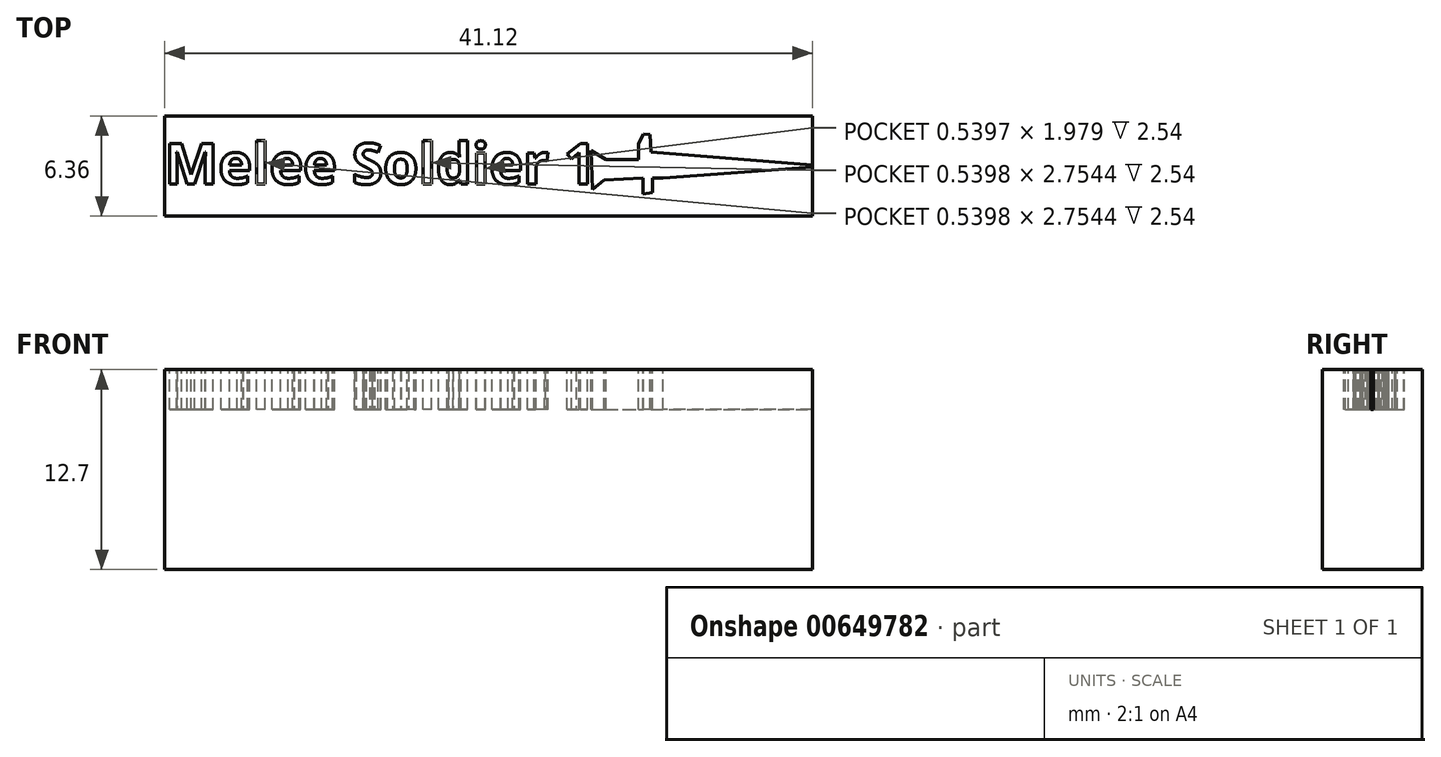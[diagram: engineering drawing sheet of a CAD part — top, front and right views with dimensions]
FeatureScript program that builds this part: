
annotation { "Feature Type Name" : "Feature", "Feature Type Description" : "" }
export const myFeature = defineFeature(function(context is Context, id is Id, definition is map)
    precondition{}
    {
        {
            var Q0;
            Q0=qCreatedBy(makeId("Top.planeOp"),FACE);
            var sketch = newSketch(context, id + "F0", { "sketchPlane" : qUnion([Q0])});
            skLineSegment(sketch, "E0.bottom", {"start": v(25.4, 3.18) * mm, "end": v(-25.4, 3.18) * mm});
            skLineSegment(sketch, "E0.top", {"start": v(25.4, -3.17) * mm, "end": v(-25.4, -3.17) * mm});
            skLineSegment(sketch, "E0.left", {"start": v(25.4, 3.18) * mm, "end": v(25.4, -3.17) * mm});
            skLineSegment(sketch, "E0.right", {"start": v(-25.4, 3.18) * mm, "end": v(-25.4, -3.17) * mm});
            skPoint(sketch, "E0.middle", {"position": v(0, 0) * mm});
            skSolve(sketch);
        }
        {
            var Q0;
            Q0 = qSketchRegion(id + "F0", true);
            extrude(context, id + "F1", {"entities" : qUnion([Q0]), "depth" : 12.7 * mm, "offsetDistance" : 25.4 * mm});
        }
        {
            var Q0;
            Q0=makeQuery(id+"F1.opExtrude","CAP_FACE",FACE,{"disambiguationData":[OSD([sQuery(id+"F0.wireOp",EDGE,"E0.bottom"),sQuery(id+"F0.wireOp",EDGE,"E0.top"),sQuery(id+"F0.wireOp",EDGE,"E0.left"),sQuery(id+"F0.wireOp",EDGE,"E0.right")])],"isStart":false});
            var sketch = newSketch(context, id + "F2", { "sketchPlane" : qUnion([Q0])});
            skLineSegment(sketch, "E1.bottom", {"start": v(-25.4, -3.17) * mm, "end": v(19.05, -3.17) * mm});
            skLineSegment(sketch, "E1.top", {"start": v(-25.4, 3.18) * mm, "end": v(19.05, 3.18) * mm});
            skLineSegment(sketch, "E1.left", {"start": v(-25.4, -3.17) * mm, "end": v(-25.4, 3.18) * mm});
            skLineSegment(sketch, "E1.right", {"start": v(19.05, -3.17) * mm, "end": v(19.05, 3.18) * mm});
            skLineSegment(sketch, "E2", {"start": v(25.4, 0) * mm, "end": v(19.05, 0) * mm});
            skSolve(sketch);
        }
        {
            var Q0;
            {var subQ3=sQuery(id+"F2.wireOp",EDGE,"E2");Q0=makeQuery(id+"F2.imprint","IMPRINT",FACE,{"disambiguationData":[TD([[makeQuery(id+"F2.imprint","IMPRINT",EDGE,{"derivedFrom":subQ3}),1.0]])]});}
            extrude(context, id + "F3", {"entities" : qUnion([Q0]), "operationType" : NewBodyOperationType.REMOVE, "oppositeDirection" : true, "depth" : 25.4 * mm, "offsetDistance" : 25.4 * mm});
        }
        {
            var Q0;
            Q0=makeQuery(id+"F3.boolean.opBoolean","COPY",FACE,{"derivedFrom":makeQuery(id+"F3.opExtrude","SWEPT_FACE",FACE,{"disambiguationData":[OSD([sQuery(id+"F2.wireOp",EDGE,"E2")])]})});
            var sketch = newSketch(context, id + "F4", { "sketchPlane" : qUnion([Q0])});
            skLineSegment(sketch, "E3", {"start": v(25.4, 8.79) * mm, "end": v(19.05, 8.79) * mm});
            skLineSegment(sketch, "E4", {"start": v(25.4, 5.16) * mm, "end": v(19.05, 5.16) * mm});
            skSolve(sketch);
        }
        {
            var Q0;
            {var subQ0=sQuery(id+"F4.wireOp",EDGE,"E3");Q0=makeQuery(id+"F4.imprint","IMPRINT",FACE,{"disambiguationData":[TD([[makeQuery(id+"F4.imprint","IMPRINT",EDGE,{"derivedFrom":subQ0}),1.0]])]});}
            var Q1;
            {var subQ0=sQuery(id+"F4.wireOp",EDGE,"E3");Q1=makeQuery(id+"F4.imprint","IMPRINT",FACE,{"disambiguationData":[TD([[makeQuery(id+"F4.imprint","IMPRINT",EDGE,{"derivedFrom":subQ0}),-1.0]])]});}
            extrude(context, id + "F5", {"entities" : qUnion([Q0, Q1]), "operationType" : NewBodyOperationType.REMOVE, "oppositeDirection" : true, "depth" : 25.4 * mm, "offsetDistance" : 25.4 * mm});
        }
        {
            var Q0;
            Q0=makeQuery(id+"F1.opExtrude","CAP_FACE",FACE,{"disambiguationData":[OSD([sQuery(id+"F0.wireOp",EDGE,"E0.bottom"),sQuery(id+"F0.wireOp",EDGE,"E0.top"),sQuery(id+"F0.wireOp",EDGE,"E0.left"),sQuery(id+"F0.wireOp",EDGE,"E0.right")])],"isStart":false});
            var sketch = newSketch(context, id + "F6", { "sketchPlane" : qUnion([Q0])});
            skText(sketch, "E5", { "text": "Melee Soldier 1", "fontName": "OpenSans-Bold.ttf"});
            const initialGuessF6  = {"E5": [-0.02336, -0.00115, 1, 0, 0.00261]};
            skSetInitialGuess(sketch, initialGuessF6);
            skSolve(sketch);
        }
        {
            var Q0;
            Q0 = qSketchRegion(id + "F6", true);
            extrude(context, id + "F7", {"entities" : qUnion([Q0]), "operationType" : NewBodyOperationType.REMOVE, "oppositeDirection" : true, "depth" : 2.54 * mm, "offsetDistance" : 25.4 * mm});
        }
        {
            var Q0;
            {var subQ0=sQuery(id+"F0.wireOp",EDGE,"E0.right");var subQ1=sQuery(id+"F0.wireOp",EDGE,"E0.top");var subQ3=sQuery(id+"F0.wireOp",EDGE,"E0.bottom");Q0=makeQuery(id+"F7.boolean.opBoolean","SPLIT",FACE,{"disambiguationData":[TD([makeQuery(id+"F1.opExtrude","SWEPT_FACE",FACE,{"disambiguationData":[OSD([subQ3])]})])],"derivedFrom":makeQuery(id+"F1.opExtrude","CAP_FACE",FACE,{"disambiguationData":[OSD([subQ3,subQ1,sQuery(id+"F0.wireOp",EDGE,"E0.left"),subQ0])],"isStart":false})});}
            var sketch = newSketch(context, id + "F8", { "sketchPlane" : qUnion([Q0])});
            skLineSegment(sketch, "E6", {"start": v(8.39, 0.81) * mm, "end": v(18.7, 0) * mm});
            skLineSegment(sketch, "E7", {"start": v(18.7, 0) * mm, "end": v(8.3, -0.76) * mm});
            skLineSegment(sketch, "E8", {"start": v(7.5, 2) * mm, "end": v(7.5, 1.77) * mm});
            skPoint(sketch, "E8.endSnap0", {"position": v(7.65, 1.68) * mm});
            skLineSegment(sketch, "E9", {"start": v(7.65, -1.68) * mm, "end": v(7.02, -1.8) * mm});
            skLineSegment(sketch, "E10", {"start": v(4.57, -0.9) * mm, "end": v(7.02, -0.78) * mm});
            skLineSegment(sketch, "E11", {"start": v(4.69, 0.78) * mm, "end": v(3.74, 0.98) * mm});
            skLineSegment(sketch, "E12", {"start": v(3.74, 0.98) * mm, "end": v(3.84, -1.5) * mm});
            skLineSegment(sketch, "E13", {"start": v(3.84, -1.5) * mm, "end": v(4.57, -0.9) * mm});
            skLineSegment(sketch, "E14", {"start": v(6.52, 0.98) * mm, "end": v(7.08, 2.03) * mm});
            skLineSegment(sketch, "E15", {"start": v(7.02, -0.78) * mm, "end": v(7.02, -1.8) * mm});
            skLineSegment(sketch, "E16", {"start": v(8.39, 0.81) * mm, "end": v(7.54, 0.88) * mm});
            skLineSegment(sketch, "E17", {"start": v(7.65, -0.78) * mm, "end": v(8.3, -0.76) * mm});
            skPoint(sketch, "E18.end.orphan", {"position": v(7.02, 0.94) * mm});
            skLineSegment(sketch, "E19", {"start": v(7.5, 2) * mm, "end": v(7.08, 2.03) * mm});
            skLineSegment(sketch, "E20", {"start": v(7.65, -1.68) * mm, "end": v(7.65, -0.78) * mm});
            skPoint(sketch, "E21.end.orphan", {"position": v(8.22, 1.32) * mm});
            skLineSegment(sketch, "E22", {"start": v(7.54, 0.88) * mm, "end": v(7.5, 1.77) * mm});
            skLineSegment(sketch, "E23", {"start": v(3.74, 0.98) * mm, "end": v(4.69, 0.4) * mm});
            skLineSegment(sketch, "E24", {"start": v(4.69, 0.4) * mm, "end": v(6.76, 0.4) * mm});
            skLineSegment(sketch, "E25", {"start": v(6.76, 0.4) * mm, "end": v(6.76, 1.43) * mm});
            skSolve(sketch);
        }
        {
            var Q0;
            Q0 = qSketchRegion(id + "F8", true);
            extrude(context, id + "F9", {"entities" : qUnion([Q0]), "operationType" : NewBodyOperationType.REMOVE, "oppositeDirection" : true, "depth" : 2.54 * mm, "offsetDistance" : 25.4 * mm});
        }
        {
            var Q0;
            {var subQ0=sQuery(id+"F0.wireOp",EDGE,"E0.right");var subQ1=sQuery(id+"F0.wireOp",EDGE,"E0.top");var subQ3=sQuery(id+"F0.wireOp",EDGE,"E0.bottom");Q0=makeQuery(id+"F7.boolean.opBoolean","SPLIT",FACE,{"disambiguationData":[TD([makeQuery(id+"F1.opExtrude","SWEPT_FACE",FACE,{"disambiguationData":[OSD([subQ3])]})])],"derivedFrom":makeQuery(id+"F1.opExtrude","CAP_FACE",FACE,{"disambiguationData":[OSD([subQ3,subQ1,sQuery(id+"F0.wireOp",EDGE,"E0.left"),subQ0])],"isStart":false})});}
            var sketch = newSketch(context, id + "F10", { "sketchPlane" : qUnion([Q0])});
            skLineSegment(sketch, "E26", {"start": v(-24.12, 3.18) * mm, "end": v(-24.12, -3.17) * mm});
            skLineSegment(sketch, "E27", {"start": v(-24.12, -3.17) * mm, "end": v(15.6, -3.17) * mm});
            skSolve(sketch);
        }
        {
            var Q0;
            {var subQ3=sQuery(id+"F10.wireOp",EDGE,"E26");Q0=makeQuery(id+"F10.imprint","IMPRINT",FACE,{"disambiguationData":[TD([[makeQuery(id+"F10.imprint","IMPRINT",EDGE,{"derivedFrom":subQ3}),1.0]])]});}
            var sketch = newSketch(context, id + "F11", { "sketchPlane" : qUnion([Q0])});
            skLineSegment(sketch, "E28", {"start": v(-23.35, -3.15) * mm, "end": v(-23.35, 3.3) * mm});
            skSolve(sketch);
        }
        {
            var Q0;
            Q0 = qSketchRegion(id + "F11", true);
            var Q1;
            {var subQ0=sQuery(id+"F10.wireOp",EDGE,"E26");Q1=makeQuery(id+"F10.imprint","IMPRINT",FACE,{"disambiguationData":[TD([[makeQuery(id+"F10.imprint","IMPRINT",EDGE,{"derivedFrom":subQ0}),-1.0]])]});}
            extrude(context, id + "F12", {"entities" : qUnion([Q0, Q1]), "operationType" : NewBodyOperationType.REMOVE, "oppositeDirection" : true, "depth" : 25.4 * mm, "offsetDistance" : 25.4 * mm});
        }
        {
            var Q0;
            {var subQ3=sQuery(id+"F10.wireOp",EDGE,"E26");Q0=makeQuery(id+"F11.imprint","IMPRINT",FACE,{"disambiguationData":[TD([[makeQuery(id+"F11.imprint","IMPRINT",EDGE,{"derivedFrom":makeQuery(id+"F10.imprint","IMPRINT",EDGE,{"derivedFrom":subQ3})}),1.0]])]});}
            var sketch = newSketch(context, id + "F13", { "sketchPlane" : qUnion([Q0])});
            skLineSegment(sketch, "E29", {"start": v(-23.34, -3.34) * mm, "end": v(-23.34, 4.75) * mm});
            skSolve(sketch);
        }
        {
            var Q0;
            {var subQ5=sQuery(id+"F10.wireOp",EDGE,"E26");var subQ8=makeQuery(id+"F11.imprint","IMPRINT",EDGE,{"derivedFrom":makeQuery(id+"F10.imprint","IMPRINT",EDGE,{"derivedFrom":subQ5})});Q0=makeQuery(id+"F13.imprint","IMPRINT",FACE,{"disambiguationData":[TD([[makeQuery(id+"F13.imprint","IMPRINT",EDGE,{"derivedFrom":subQ8}),1.0]])]});}
            extrude(context, id + "F14", {"entities" : qUnion([Q0]), "operationType" : NewBodyOperationType.REMOVE, "oppositeDirection" : true, "depth" : 25.4 * mm, "offsetDistance" : 25.4 * mm});
        }
        {
            var Q0;
            Q0=makeQuery(id+"F1.opExtrude","SWEPT_FACE",FACE,{"disambiguationData":[OSD([sQuery(id+"F0.wireOp",EDGE,"E0.left")])]});
            var sketch = newSketch(context, id + "F15", { "sketchPlane" : qUnion([Q0])});
            skLineSegment(sketch, "E30.bottom", {"start": v(-8.17, -4.06) * mm, "end": v(13.24, -4.06) * mm});
            skLineSegment(sketch, "E30.top", {"start": v(-8.17, 19.38) * mm, "end": v(13.24, 19.38) * mm});
            skLineSegment(sketch, "E30.left", {"start": v(-8.17, -4.06) * mm, "end": v(-8.17, 19.38) * mm});
            skLineSegment(sketch, "E30.right", {"start": v(13.24, -4.06) * mm, "end": v(13.24, 19.38) * mm});
            skSolve(sketch);
        }
        {
            var Q0;
            Q0 = qSketchRegion(id + "F15", true);
            extrude(context, id + "F16", {"entities" : qUnion([Q0]), "operationType" : NewBodyOperationType.REMOVE, "oppositeDirection" : true, "depth" : 7.62 * mm, "offsetDistance" : 25.4 * mm});
        }
    });
